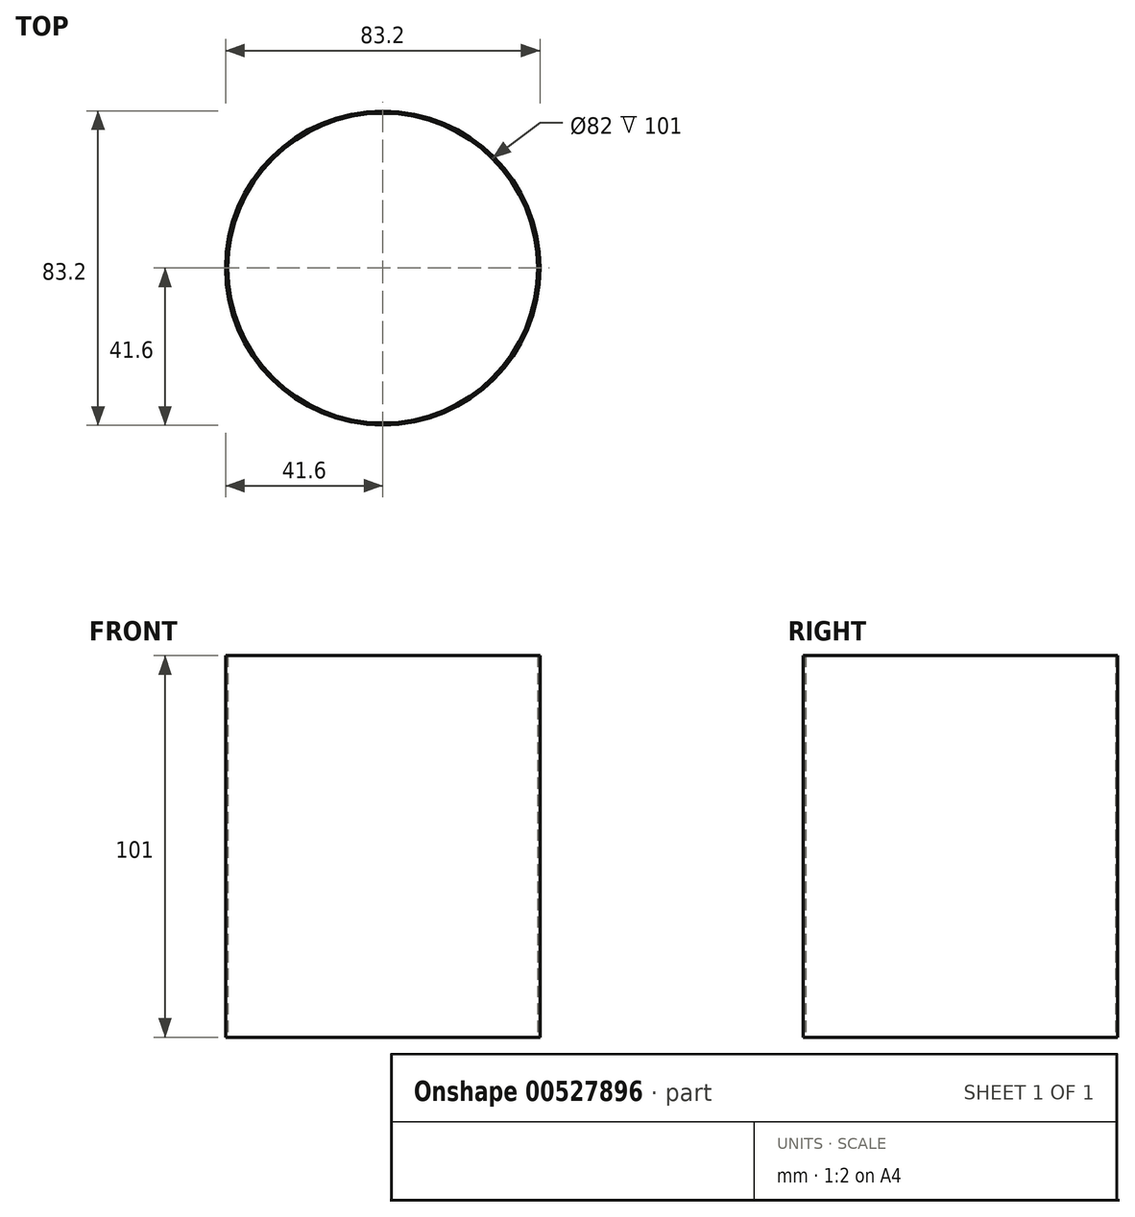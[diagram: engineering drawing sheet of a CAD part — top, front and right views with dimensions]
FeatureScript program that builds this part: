
annotation { "Feature Type Name" : "Feature", "Feature Type Description" : "" }
export const myFeature = defineFeature(function(context is Context, id is Id, definition is map)
    precondition{}
    {
        {
            var Q0;
            Q0=qCreatedBy(makeId("Top.planeOp"),FACE);
            var sketch = newSketch(context, id + "F0", { "sketchPlane" : qUnion([Q0])});
            skCircle(sketch, "E0", {"center": v(0, 0) * mm, "radius": 41 * mm});
            skCircle(sketch, "E1.0", {"center": v(0, 0) * mm, "radius": 41.6 * mm});
            skSolve(sketch);
        }
        {
            var Q0;
            Q0=qSketchRegion(id+"F0",true);
            extrude(context, id + "F1", {"entities" : qUnion([Q0]), "depth" : 101 * mm});
        }
    });
